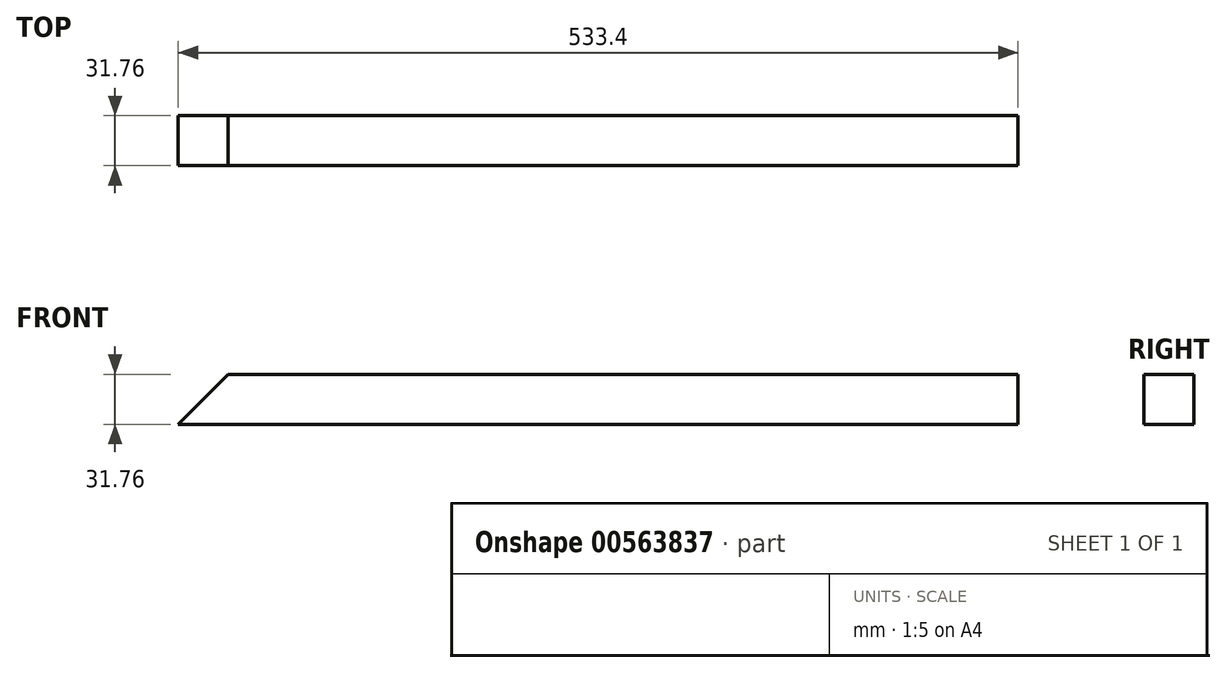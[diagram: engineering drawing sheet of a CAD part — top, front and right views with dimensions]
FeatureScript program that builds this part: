
annotation { "Feature Type Name" : "Feature", "Feature Type Description" : "" }
export const myFeature = defineFeature(function(context is Context, id is Id, definition is map)
    precondition{}
    {
        {
            var Q0;
            Q0=qCreatedBy(makeId("Front.planeOp"),FACE);
            var sketch = newSketch(context, id + "F0", { "sketchPlane" : qUnion([Q0])});
            skLineSegment(sketch, "E0.bottom", {"start": v(-266.7, 15.88) * mm, "end": v(266.7, 15.88) * mm});
            skLineSegment(sketch, "E0.top", {"start": v(-266.7, -15.88) * mm, "end": v(266.7, -15.88) * mm});
            skLineSegment(sketch, "E0.left", {"start": v(-266.7, 15.88) * mm, "end": v(-266.7, -15.88) * mm});
            skLineSegment(sketch, "E0.right", {"start": v(266.7, 15.88) * mm, "end": v(266.7, -15.88) * mm});
            skPoint(sketch, "E0.middle", {"position": v(0, 0) * mm});
            skLineSegment(sketch, "E1", {"start": v(-266.7, -15.88) * mm, "end": v(-234.95, 15.87) * mm});
            skSolve(sketch);
        }
        {
            var Q0;
            Q0=makeQuery(id+"F0.imprint","IMPRINT",FACE,{"disambiguationData":[TD([[makeQuery(id+"F0.imprint","IMPRINT",EDGE,{"derivedFrom":sQuery(id+"F0.wireOp",EDGE,"E0.top")}),1.0]])]});
            extrude(context, id + "F1", {"entities" : qUnion([Q0]), "endBound" : BoundingType.SYMMETRIC, "depth" : 31.75 * mm, "offsetDistance" : 25.4 * mm});
        }
    });
